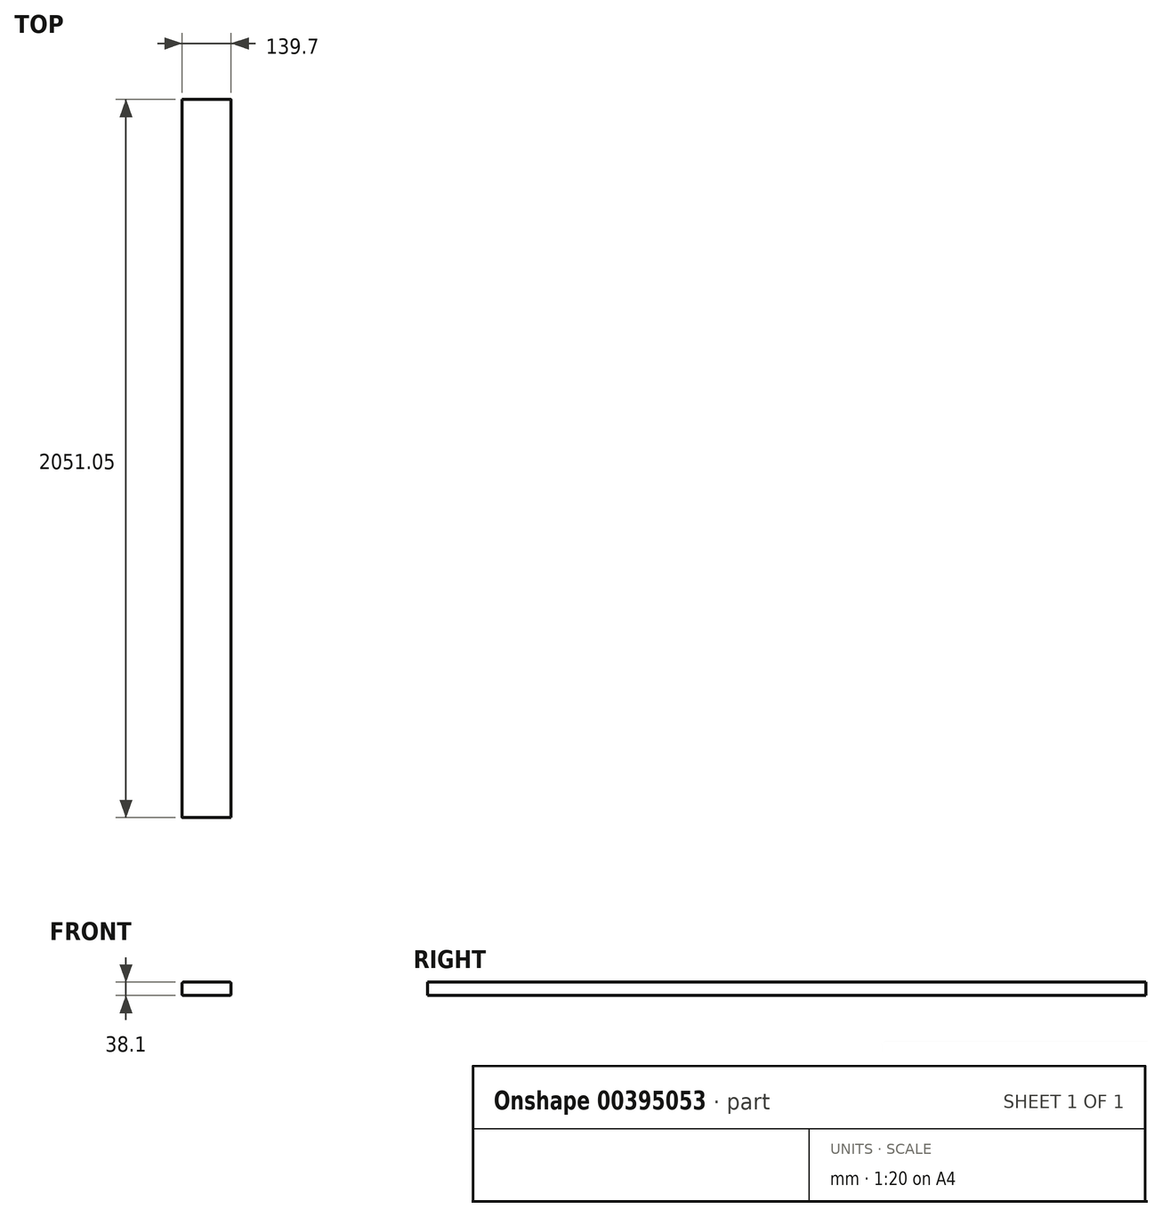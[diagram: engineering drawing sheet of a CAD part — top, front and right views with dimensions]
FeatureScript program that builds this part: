
annotation { "Feature Type Name" : "Feature", "Feature Type Description" : "" }
export const myFeature = defineFeature(function(context is Context, id is Id, definition is map)
    precondition{}
    {
        {
            var Q0;
            Q0=qCreatedBy(makeId("Front.planeOp"),FACE);
            var sketch = newSketch(context, id + "F0", { "sketchPlane" : qUnion([Q0])});
            skLineSegment(sketch, "E0.bottom", {"start": v(3.18, 0) * mm, "end": v(136.52, 0) * mm});
            skLineSegment(sketch, "E0.top", {"start": v(3.17, 38.1) * mm, "end": v(136.53, 38.1) * mm});
            skLineSegment(sketch, "E0.left", {"start": v(0, 3.18) * mm, "end": v(0, 34.93) * mm});
            skLineSegment(sketch, "E0.right", {"start": v(139.7, 3.18) * mm, "end": v(139.7, 34.93) * mm});
            skPoint(sketch, "E1.visualSharp", {"position": v(0, 38.1) * mm});
            skArc(sketch, "E1.filletArc", {"start": v(3.17, 38.1) * mm, "mid": v(0.93, 37.17) * mm, "end": v(0, 34.93) * mm});
            skPoint(sketch, "E2.visualSharp", {"position": v(0, 0) * mm});
            skArc(sketch, "E2.filletArc", {"start": v(0, 3.18) * mm, "mid": v(0.93, 0.93) * mm, "end": v(3.18, 0) * mm});
            skPoint(sketch, "E3.visualSharp", {"position": v(139.7, 0) * mm});
            skArc(sketch, "E3.filletArc", {"start": v(136.52, 0) * mm, "mid": v(138.77, 0.93) * mm, "end": v(139.7, 3.18) * mm});
            skPoint(sketch, "E4.visualSharp", {"position": v(139.7, 38.1) * mm});
            skArc(sketch, "E4.filletArc", {"start": v(139.7, 34.93) * mm, "mid": v(138.77, 37.17) * mm, "end": v(136.53, 38.1) * mm});
            skSolve(sketch);
        }
        {
            var Q0;
            Q0 = qSketchRegion(id + "F0", true);
            extrude(context, id + "F1", {"entities" : qUnion([Q0]), "depth" : 2051.05 * mm});
        }
    });
